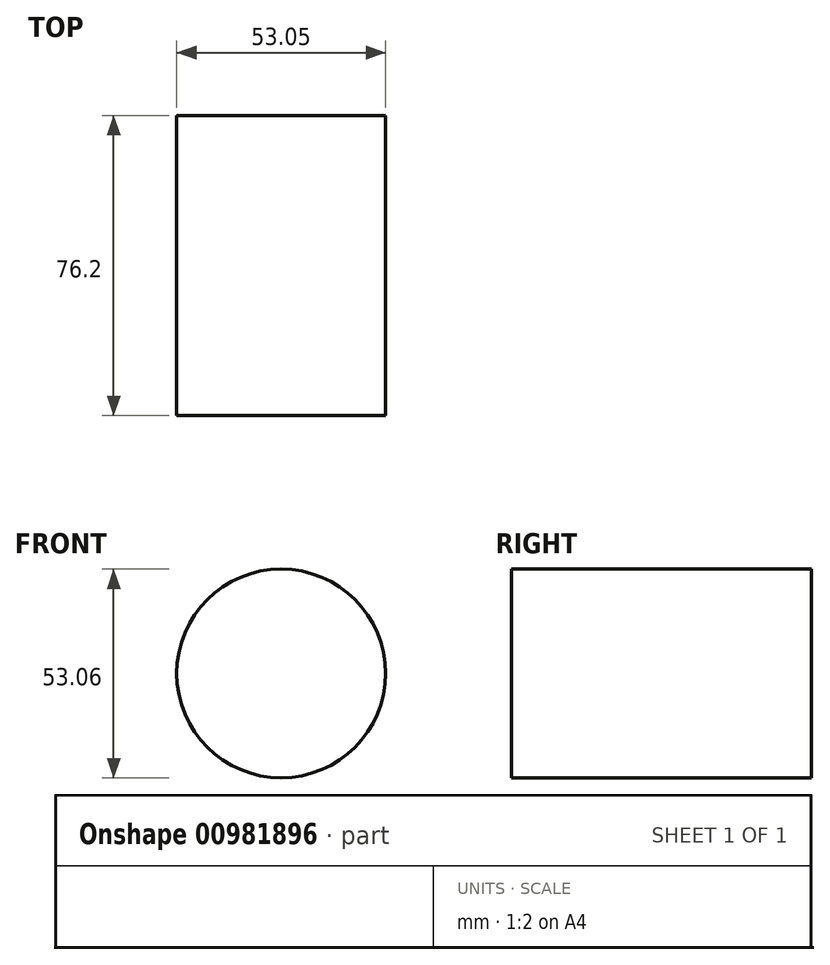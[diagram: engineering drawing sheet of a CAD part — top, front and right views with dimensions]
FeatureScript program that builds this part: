
annotation { "Feature Type Name" : "Feature", "Feature Type Description" : "" }
export const myFeature = defineFeature(function(context is Context, id is Id, definition is map)
    precondition{}
    {
        {
            var Q0;
            Q0=qCreatedBy(makeId("Front.planeOp"),FACE);
            var sketch = newSketch(context, id + "F0", { "sketchPlane" : qUnion([Q0])});
            skCircle(sketch, "E0", {"center": v(-25.85, 25.73) * mm, "radius": 26.53 * mm});
            skSolve(sketch);
        }
        {
            var Q0;
            Q0=makeQuery(id+"F0.imprint","IMPRINT",FACE,{"disambiguationData":[TD([[makeQuery(id+"F0.imprint","IMPRINT",EDGE,{"derivedFrom":sQuery(id+"F0.wireOp",EDGE,"E0")}),1.0]])]});
            extrude(context, id + "F1", {"entities" : qUnion([Q0]), "depth" : 76.2 * mm, "offsetDistance" : 25.4 * mm});
        }
    });
